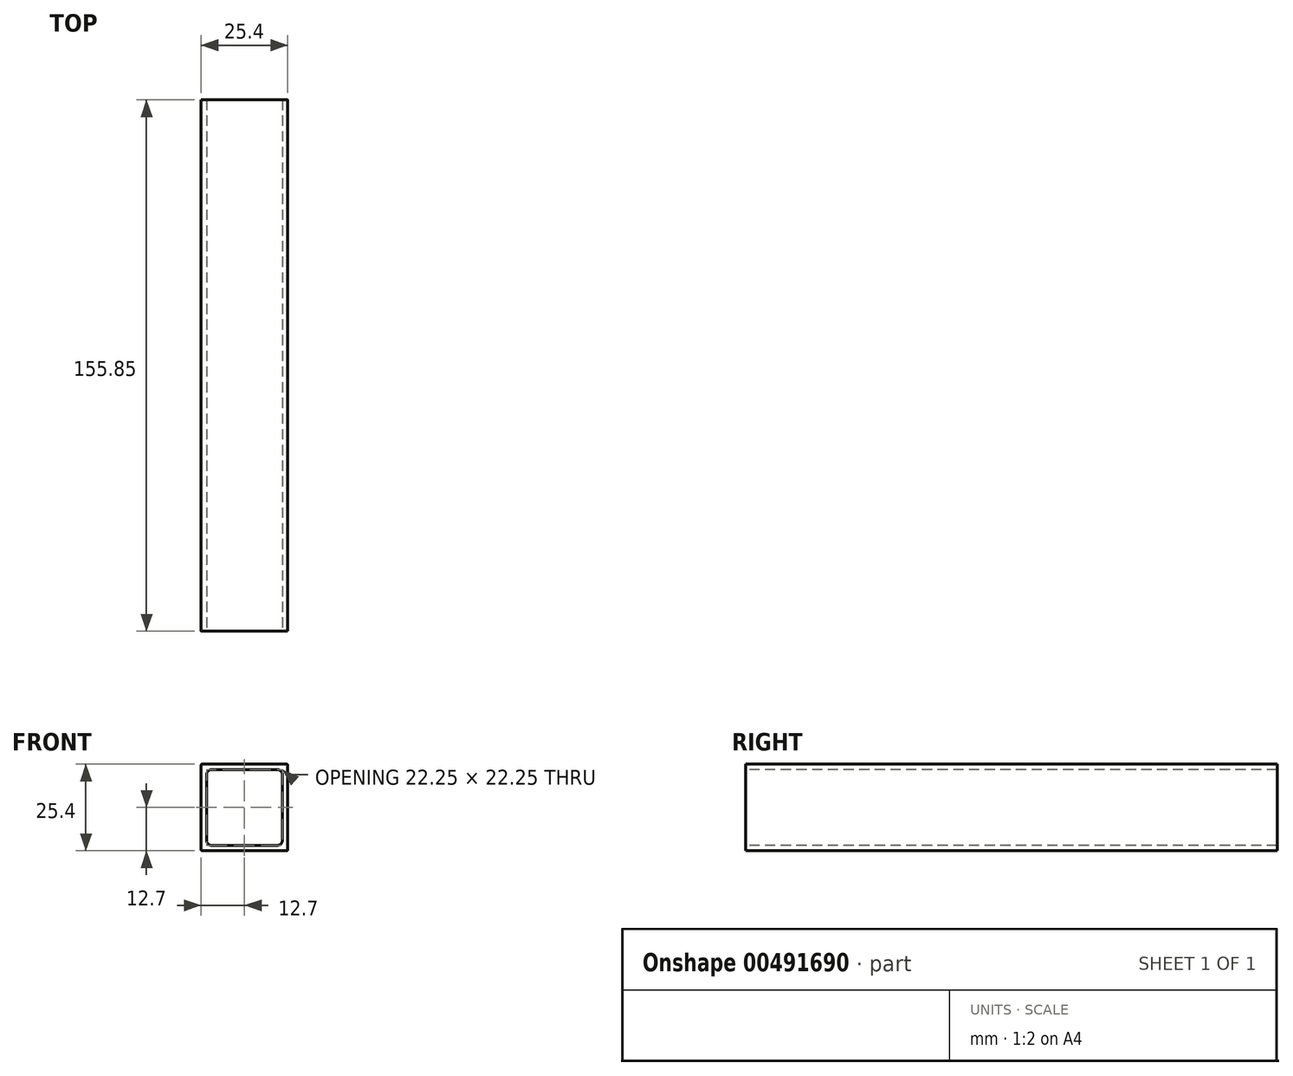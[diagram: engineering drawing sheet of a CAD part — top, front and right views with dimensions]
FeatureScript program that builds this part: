
annotation { "Feature Type Name" : "Feature", "Feature Type Description" : "" }
export const myFeature = defineFeature(function(context is Context, id is Id, definition is map)
    precondition{}
    {
        {
            var Q0;
            Q0=qCreatedBy(makeId("Front.planeOp"),FACE);
            var sketch = newSketch(context, id + "F0", { "sketchPlane" : qUnion([Q0])});
            skLineSegment(sketch, "E0.bottom", {"start": v(12.7, 12.7) * mm, "end": v(-12.7, 12.7) * mm});
            skLineSegment(sketch, "E0.top", {"start": v(12.7, -12.7) * mm, "end": v(-12.7, -12.7) * mm});
            skLineSegment(sketch, "E0.left", {"start": v(12.7, 12.7) * mm, "end": v(12.7, -12.7) * mm});
            skLineSegment(sketch, "E0.right", {"start": v(-12.7, 12.7) * mm, "end": v(-12.7, -12.7) * mm});
            skPoint(sketch, "E0.middle", {"position": v(0, 0) * mm});
            skSolve(sketch);
        }
        {
            var Q0;
            Q0=qSketchRegion(id+"F0",true);
            extrude(context, id + "F1", {"entities" : qUnion([Q0]), "depth" : 155.85 * mm, "offsetDistance" : 25.4 * mm});
        }
        {
            var Q0;
            Q0=makeQuery(id+"F1.opExtrude","CAP_FACE",FACE,{"disambiguationData":[OSD([sQuery(id+"F0.wireOp",EDGE,"E0.bottom"),sQuery(id+"F0.wireOp",EDGE,"E0.top"),sQuery(id+"F0.wireOp",EDGE,"E0.left"),sQuery(id+"F0.wireOp",EDGE,"E0.right")])],"isStart":false});
            var sketch = newSketch(context, id + "F2", { "sketchPlane" : qUnion([Q0])});
            skLineSegment(sketch, "E1.bottom", {"start": v(-11.13, 11.13) * mm, "end": v(11.13, 11.13) * mm});
            skLineSegment(sketch, "E1.top", {"start": v(-11.13, -11.13) * mm, "end": v(11.13, -11.13) * mm});
            skLineSegment(sketch, "E1.left", {"start": v(-11.13, 11.13) * mm, "end": v(-11.13, -11.13) * mm});
            skLineSegment(sketch, "E1.right", {"start": v(11.13, 11.13) * mm, "end": v(11.13, -11.13) * mm});
            skPoint(sketch, "E1.middle", {"position": v(0, 0) * mm});
            skSolve(sketch);
        }
        {
            var Q0;
            Q0=qSketchRegion(id+"F2",true);
            extrude(context, id + "F3", {"entities" : qUnion([Q0]), "operationType" : NewBodyOperationType.REMOVE, "endBound" : BoundingType.UP_TO_NEXT, "oppositeDirection" : true, "depth" : 25.4 * mm});
        }
        {
            var Q0;
            Q0=makeQuery(id+"F3.boolean.opBoolean","COPY",EDGE,{"derivedFrom":makeQuery(id+"F3.opExtrude","SWEPT_EDGE",EDGE,{"disambiguationData":[OSD([sQuery(id+"F2.wireOp",EDGE,"E1.bottom"),sQuery(id+"F2.wireOp",EDGE,"E1.left")])]})});
            var Q1;
            Q1=makeQuery(id+"F3.boolean.opBoolean","COPY",EDGE,{"derivedFrom":makeQuery(id+"F3.opExtrude","SWEPT_EDGE",EDGE,{"disambiguationData":[OSD([sQuery(id+"F2.wireOp",EDGE,"E1.top"),sQuery(id+"F2.wireOp",EDGE,"E1.right")])]})});
            var Q2;
            Q2=makeQuery(id+"F3.boolean.opBoolean","COPY",EDGE,{"derivedFrom":makeQuery(id+"F3.opExtrude","SWEPT_EDGE",EDGE,{"disambiguationData":[OSD([sQuery(id+"F2.wireOp",EDGE,"E1.bottom"),sQuery(id+"F2.wireOp",EDGE,"E1.right")])]})});
            var Q3;
            Q3=makeQuery(id+"F3.boolean.opBoolean","COPY",EDGE,{"derivedFrom":makeQuery(id+"F3.opExtrude","SWEPT_EDGE",EDGE,{"disambiguationData":[OSD([sQuery(id+"F2.wireOp",EDGE,"E1.top"),sQuery(id+"F2.wireOp",EDGE,"E1.left")])]})});
            fillet(context, id + "F4", {"entities" : qUnion([Q0, Q1, Q2, Q3]), "radius" : 1.52 * mm, "tangentPropagation" : true, "allowEdgeOverflow" : false});
        }
        {
            var Q0;
            Q0=makeQuery(id+"F1.opExtrude","SWEPT_EDGE",EDGE,{"disambiguationData":[OSD([sQuery(id+"F0.wireOp",EDGE,"E0.bottom"),sQuery(id+"F0.wireOp",EDGE,"E0.left")])]});
            var Q1;
            Q1=makeQuery(id+"F1.opExtrude","SWEPT_EDGE",EDGE,{"disambiguationData":[OSD([sQuery(id+"F0.wireOp",EDGE,"E0.top"),sQuery(id+"F0.wireOp",EDGE,"E0.left")])]});
            var Q2;
            Q2=makeQuery(id+"F1.opExtrude","SWEPT_EDGE",EDGE,{"disambiguationData":[OSD([sQuery(id+"F0.wireOp",EDGE,"E0.top"),sQuery(id+"F0.wireOp",EDGE,"E0.right")])]});
            var Q3;
            Q3=makeQuery(id+"F1.opExtrude","SWEPT_EDGE",EDGE,{"disambiguationData":[OSD([sQuery(id+"F0.wireOp",EDGE,"E0.bottom"),sQuery(id+"F0.wireOp",EDGE,"E0.right")])]});
            fillet(context, id + "F5", {"entities" : qUnion([Q0, Q1, Q2, Q3]), "radius" : 0.25 * mm, "tangentPropagation" : true, "allowEdgeOverflow" : false});
        }
    });
